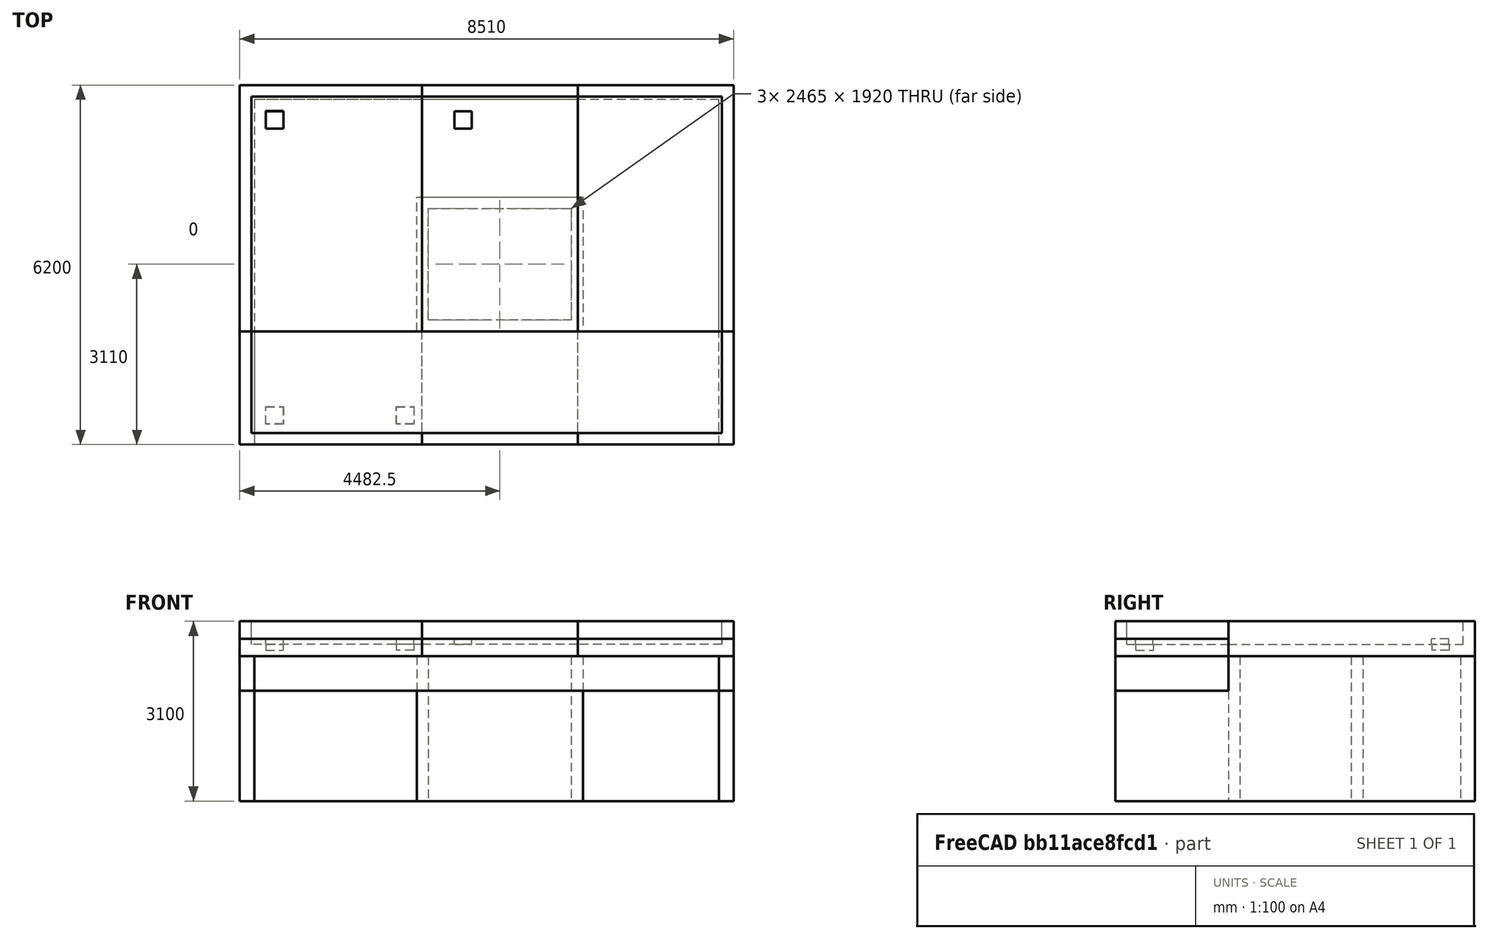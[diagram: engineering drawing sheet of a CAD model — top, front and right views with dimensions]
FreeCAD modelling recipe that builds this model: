
FCSTD DOCUMENT  (FreeCAD 0.21R33694 (Git))
Label: swimmingPool
License: All rights reserved
LicenseURL: http://en.wikipedia.org/wiki/All_rights_reserved
objects: Part::Feature×13, Part::FeaturePython×11, Sketcher::SketchObject×10, Part::Extrusion×10, Image::ImagePlane×3, Part::MultiFuse×3, App::MaterialObjectPython×3, Part::Compound×2, Part::Box×2, Fem::FeaturePython×1, Fem::FemSolverObjectPython×1, Fem::ConstraintFixed×1, Fem::ConstraintForce×1, App::DocumentObjectGroup×1, Fem::FemMeshObjectPython×1, Fem::FemAnalysis×1
note: 51 computed .brp shape members not serialized (recipe doc carries the construction recipe); baked Part::Feature solids carry a one-line shape summary decoded from their .brp

FEATURE [Image::ImagePlane] ImagePlane  label="draufsicht_trh1"
  Placement = pos=(3803,2748,-500) rot=(0,0,1;0rad)
  XSize = 14030.6
  YSize = 11281.2
  expr: XSize = 321.5 * 43.641 mm
  expr: YSize = 258.5 * 43.641 mm
FEATURE [Image::ImagePlane] ImagePlane001  label="grundriss_trh1"
  Placement = pos=(4033,1694,-1000) rot=(0,0,1;0rad)
  XSize = 13245
  YSize = 11006.3
  expr: XSize = 303.5 * 43.641 mm
  expr: YSize = 252.2 * 43.641 mm
FEATURE [Sketcher::SketchObject] Sketch
  FullyConstrained = true
  sketch-geometry (12):
    g0: LineSegment StartX=3050 StartY=4270 StartZ=0 EndX=5915 EndY=4270 EndZ=0
    g1: LineSegment StartX=5915 StartY=4270 StartZ=0 EndX=5915 EndY=1950 EndZ=0
    g2: LineSegment StartX=5915 StartY=1950 StartZ=0 EndX=3050 EndY=1950 EndZ=0
    g3: LineSegment StartX=3050 StartY=1950 StartZ=0 EndX=3050 EndY=4270 EndZ=0
    g4: LineSegment StartX=3250 StartY=4070 StartZ=0 EndX=5715 EndY=4070 EndZ=0
    g5: LineSegment StartX=5715 StartY=4070 StartZ=0 EndX=5715 EndY=2150 EndZ=0
    g6: LineSegment StartX=5715 StartY=2150 StartZ=0 EndX=3250 EndY=2150 EndZ=0
    g7: LineSegment StartX=3250 StartY=2150 StartZ=0 EndX=3250 EndY=4070 EndZ=0
    g8: LineSegment StartX=5715 StartY=4070 StartZ=0 EndX=5715 EndY=4270 EndZ=0
    g9: LineSegment StartX=5715 StartY=2150 StartZ=0 EndX=5715 EndY=1950 EndZ=0
    g10: LineSegment StartX=3250 StartY=2150 StartZ=0 EndX=3050 EndY=2150 EndZ=0
    g11: LineSegment StartX=5715 StartY=2150 StartZ=0 EndX=5915 EndY=2150 EndZ=0
  constraints (36):
    c: Coincident(g0,g1)
    c: Coincident(g1,g2)
    c: Coincident(g2,g3)
    c: Coincident(g3,g0)
    c: Horizontal(g0)
    c: Horizontal(g2)
    c: Vertical(g1)
    c: Vertical(g3)
    c: DistanceY(g-1,g2) = 1950
    c: DistanceX(g0,g0) = 2865
    c: DistanceY(g3,g3) = 2320
    c: Coincident(g4,g5)
    c: Coincident(g5,g6)
    c: Coincident(g6,g7)
    c: Coincident(g7,g4)
    c: Horizontal(g4)
    c: Horizontal(g6)
    c: Vertical(g5)
    c: Vertical(g7)
    c: Coincident(g8,g4)
    c: PointOnObject(g8,g0)
    c: Vertical(g8)
    c: Coincident(g9,g5)
    c: PointOnObject(g9,g2)
    c: Vertical(g9)
    c: Coincident(g10,g6)
    c: PointOnObject(g10,g3)
    c: Coincident(g11,g5)
    c: PointOnObject(g11,g1)
    c: Horizontal(g11)
    c: Horizontal(g10)
    c: Equal(g10,g11)
    c: Equal(g11,g9)
    c: Equal(g9,g8)
    c: DistanceX(g-1,g2) = 3050
    c: DistanceX(g11,g11) = 200
FEATURE [Part::Extrusion] Extrude  label="Fahrstuhlschacht"
  Base = -> Sketch
  Dir = (0,0,-1)
  DirMode = 0
  FaceMakerClass = Part::FaceMakerBullseye
  LengthFwd = 2500
  LengthRev = 0
  Solid = true
  Symmetric = false
FEATURE [Image::ImagePlane] ImagePlane002  label="gwp"
  Placement = pos=(4190,2670,390) rot=(0,0,1;0rad)
  XSize = 9203.05
  YSize = 7710.83
  expr: XSize = 298.5 * 30.831 mm
  expr: YSize = 250.1 * 30.831 mm
FEATURE [Sketcher::SketchObject] Sketch001
  ExternalGeometry = -> [Extrude]
  FullyConstrained = true
  MapMode = 5
  Support = -> [Extrude]
  sketch-geometry (4):
    g0: LineSegment StartX=0 StartY=0 StartZ=0 EndX=3140 EndY=0 EndZ=0
    g1: LineSegment StartX=3140 StartY=0 StartZ=0 EndX=3140 EndY=6200 EndZ=0
    g2: LineSegment StartX=3140 StartY=6200 StartZ=0 EndX=0 EndY=6200 EndZ=0
    g3: LineSegment StartX=0 StartY=6200 StartZ=0 EndX=0 EndY=0 EndZ=0
  constraints (11):
    c: Coincident(g0,g1)
    c: Coincident(g1,g2)
    c: Coincident(g2,g3)
    c: Coincident(g3,g0)
    c: Horizontal(g0)
    c: Horizontal(g2)
    c: Vertical(g1)
    c: Vertical(g3)
    c: Coincident(g0,g-1)
    c: DistanceX(g0,g0) = 3140
    c: DistanceY(g3,g3) = 6200
FEATURE [Part::Extrusion] Extrude001
  Base = -> Sketch001
  Dir = (0,0,1)
  DirMode = 0
  FaceMakerClass = Part::FaceMakerBullseye
  LengthFwd = 200
  LengthRev = 0
  Solid = true
  Symmetric = false
FEATURE [Sketcher::SketchObject] Sketch002
  ExternalGeometry = -> [Extrude001]
  FullyConstrained = true
  MapMode = 5
  Support = -> [Extrude]
  sketch-geometry (5):
    g0: LineSegment StartX=5825 StartY=6200 StartZ=0 EndX=8510 EndY=6200 EndZ=0
    g1: LineSegment StartX=8510 StartY=6200 StartZ=0 EndX=8510 EndY=0 EndZ=0
    g2: LineSegment StartX=8510 StartY=0 StartZ=0 EndX=5825 EndY=0 EndZ=0
    g3: LineSegment StartX=5825 StartY=0 StartZ=0 EndX=5825 EndY=6200 EndZ=0
    g4: LineSegment StartX=3140 StartY=0 StartZ=0 EndX=5825 EndY=0 EndZ=0
  constraints (14):
    c: Coincident(g0,g1)
    c: Coincident(g1,g2)
    c: Coincident(g2,g3)
    c: Coincident(g3,g0)
    c: Horizontal(g0)
    c: Horizontal(g2)
    c: Vertical(g1)
    c: Vertical(g3)
    c: Horizontal(g2,g-3)
    c: Equal(g-4,g1)
    c: Coincident(g4,g-3)
    c: Coincident(g4,g2)
    c: Equal(g4,g2)
    c: DistanceX(g-4,g1) = 8510
FEATURE [Part::Extrusion] Extrude002
  Base = -> Sketch002
  Dir = (0,0,1)
  DirMode = 0
  FaceMakerClass = Part::FaceMakerBullseye
  LengthFwd = 200
  LengthRev = 0
  Solid = true
  Symmetric = false
FEATURE [Sketcher::SketchObject] Sketch003
  ExternalGeometry = -> [Extrude001,Extrude002]
  FullyConstrained = true
  MapMode = 5
  Support = -> [Extrude]
  sketch-geometry (4):
    g0: LineSegment StartX=3140 StartY=6200 StartZ=0 EndX=5825 EndY=6200 EndZ=0
    g1: LineSegment StartX=5825 StartY=6200 StartZ=0 EndX=5825 EndY=0 EndZ=0
    g2: LineSegment StartX=5825 StartY=0 StartZ=0 EndX=3140 EndY=0 EndZ=0
    g3: LineSegment StartX=3140 StartY=0 StartZ=0 EndX=3140 EndY=6200 EndZ=0
  constraints (10):
    c: Coincident(g0,g1)
    c: Coincident(g1,g2)
    c: Coincident(g2,g3)
    c: Coincident(g3,g0)
    c: Horizontal(g0)
    c: Horizontal(g2)
    c: Vertical(g1)
    c: Vertical(g3)
    c: Coincident(g0,g-3)
    c: Coincident(g1,g-4)
FEATURE [Part::Extrusion] Extrude003
  Base = -> Sketch003
  Dir = (0,0,1)
  DirMode = 0
  FaceMakerClass = Part::FaceMakerBullseye
  LengthFwd = 200
  LengthRev = 0
  Solid = true
  Symmetric = false
FEATURE [Sketcher::SketchObject] Sketch004
  ExternalGeometry = -> [Extrude001]
  FullyConstrained = true
  MapMode = 5
  Placement = pos=(0,0,200) rot=(0,0,1;0rad)
  Support = -> [Extrude001]
  sketch-geometry (8):
    g0: LineSegment StartX=0 StartY=0 StartZ=0 EndX=0 EndY=6200 EndZ=0
    g1: LineSegment StartX=0 StartY=6200 StartZ=0 EndX=3140 EndY=6200 EndZ=0
    g2: LineSegment StartX=3140 StartY=6200 StartZ=0 EndX=3140 EndY=6000 EndZ=0
    g3: LineSegment StartX=3140 StartY=6000 StartZ=0 EndX=200 EndY=6000 EndZ=0
    g4: LineSegment StartX=200 StartY=6000 StartZ=0 EndX=200 EndY=200 EndZ=0
    g5: LineSegment StartX=200 StartY=200 StartZ=0 EndX=3140 EndY=200 EndZ=0
    g6: LineSegment StartX=3140 StartY=200 StartZ=0 EndX=3140 EndY=0 EndZ=0
    g7: LineSegment StartX=3140 StartY=0 StartZ=0 EndX=0 EndY=0 EndZ=0
  constraints (21):
    c: Coincident(g-1,g0)
    c: Coincident(g0,g1)
    c: Coincident(g1,g2)
    c: Vertical(g2)
    c: Coincident(g2,g3)
    c: Horizontal(g3)
    c: Coincident(g3,g4)
    c: Vertical(g4)
    c: Coincident(g4,g5)
    c: Coincident(g5,g6)
    c: PointOnObject(g6,g-1)
    c: Vertical(g6)
    c: Coincident(g6,g7)
    c: Coincident(g7,g0)
    c: Horizontal(g5)
    c: Coincident(g0,g-3)
    c: Coincident(g1,g-3)
    c: Equal(g7,g1)
    c: Equal(g2,g6)
    c: DistanceY(g2,g2) = 200
    c: DistanceX(g0,g4) = 200
FEATURE [Part::Extrusion] Extrude004
  Base = -> Sketch004
  Dir = (0,0,1)
  DirMode = 0
  FaceMakerClass = Part::FaceMakerBullseye
  LengthFwd = 400
  LengthRev = 0
  Solid = true
  Symmetric = false
FEATURE [Part::MultiFuse] Fusion  label="trog_links"
  Refine = true
  Shapes = -> [Extrude001,Extrude004]
FEATURE [Sketcher::SketchObject] Sketch005
  ExternalGeometry = -> [Extrude002]
  FullyConstrained = true
  MapMode = 5
  Placement = pos=(0,0,200) rot=(0,0,1;0rad)
  Support = -> [Extrude002]
  sketch-geometry (8):
    g0: LineSegment StartX=5825 StartY=6200 StartZ=0 EndX=8510 EndY=6200 EndZ=0
    g1: LineSegment StartX=8510 StartY=6200 StartZ=0 EndX=8510 EndY=0 EndZ=0
    g2: LineSegment StartX=8510 StartY=0 StartZ=0 EndX=5825 EndY=0 EndZ=0
    g3: LineSegment StartX=5825 StartY=0 StartZ=0 EndX=5825 EndY=200 EndZ=0
    g4: LineSegment StartX=5825 StartY=200 StartZ=0 EndX=8310 EndY=200 EndZ=0
    g5: LineSegment StartX=8310 StartY=200 StartZ=0 EndX=8310 EndY=6000 EndZ=0
    g6: LineSegment StartX=8310 StartY=6000 StartZ=0 EndX=5825 EndY=6000 EndZ=0
    g7: LineSegment StartX=5825 StartY=6000 StartZ=0 EndX=5825 EndY=6200 EndZ=0
  constraints (22):
    c: Coincident(g-3,g0)
    c: Coincident(g0,g-3)
    c: Coincident(g0,g1)
    c: PointOnObject(g1,g-1)
    c: Vertical(g1)
    c: Coincident(g1,g2)
    c: PointOnObject(g2,g-1)
    c: Coincident(g2,g3)
    c: Coincident(g3,g4)
    c: Coincident(g4,g5)
    c: Coincident(g5,g6)
    c: Coincident(g6,g7)
    c: Coincident(g7,g0)
    c: Vertical(g7)
    c: Horizontal(g6)
    c: Horizontal(g4)
    c: Vertical(g5)
    c: Vertical(g3)
    c: Equal(g2,g0)
    c: Equal(g7,g3)
    c: DistanceY(g3,g3) = 200
    c: DistanceX(g4,g1) = 200
FEATURE [Part::Extrusion] Extrude005
  Base = -> Sketch005
  Dir = (0,0,1)
  DirMode = 0
  FaceMakerClass = Part::FaceMakerBullseye
  LengthFwd = 400
  LengthRev = 0
  Solid = true
  Symmetric = false
FEATURE [Part::MultiFuse] Fusion001  label="trog_rechts"
  Refine = true
  Shapes = -> [Extrude005,Extrude002]
FEATURE [Sketcher::SketchObject] Sketch006
  ExternalGeometry = -> [Extrude003]
  FullyConstrained = true
  MapMode = 5
  Placement = pos=(0,0,200) rot=(0,0,1;0rad)
  Support = -> [Extrude003]
  sketch-geometry (8):
    g0: LineSegment StartX=3140 StartY=6200 StartZ=0 EndX=5825 EndY=6200 EndZ=0
    g1: LineSegment StartX=5825 StartY=6200 StartZ=0 EndX=5825 EndY=6000 EndZ=0
    g2: LineSegment StartX=5825 StartY=6000 StartZ=0 EndX=3140 EndY=6000 EndZ=0
    g3: LineSegment StartX=3140 StartY=6000 StartZ=0 EndX=3140 EndY=6200 EndZ=0
    g4: LineSegment StartX=3140 StartY=0 StartZ=0 EndX=5825 EndY=0 EndZ=0
    g5: LineSegment StartX=5825 StartY=0 StartZ=0 EndX=5825 EndY=200 EndZ=0
    g6: LineSegment StartX=5825 StartY=200 StartZ=0 EndX=3140 EndY=200 EndZ=0
    g7: LineSegment StartX=3140 StartY=200 StartZ=0 EndX=3140 EndY=0 EndZ=0
  constraints (22):
    c: Coincident(g0,g1)
    c: Coincident(g1,g2)
    c: Coincident(g2,g3)
    c: Coincident(g3,g0)
    c: Horizontal(g2)
    c: Vertical(g1)
    c: Vertical(g3)
    c: Coincident(g0,g-3)
    c: Coincident(g0,g-3)
    c: DistanceY(g1,g1) = 200
    c: Coincident(g4,g5)
    c: Coincident(g5,g6)
    c: Coincident(g6,g7)
    c: Coincident(g7,g4)
    c: Horizontal(g4)
    c: Horizontal(g6)
    c: Vertical(g5)
    c: Vertical(g7)
    c: PointOnObject(g4,g-1)
    c: Vertical(g6,g2)
    c: Equal(g6,g2)
    c: Equal(g5,g1)
FEATURE [Part::Extrusion] Extrude006
  Base = -> Sketch006
  Dir = (0,0,1)
  DirMode = 0
  FaceMakerClass = Part::FaceMakerBullseye
  LengthFwd = 400
  LengthRev = 0
  Solid = true
  Symmetric = false
FEATURE [Part::MultiFuse] Fusion002  label="trog_mitte"
  Refine = true
  Shapes = -> [Extrude006,Extrude003]
FEATURE [Sketcher::SketchObject] Sketch007
  ExternalGeometry = -> [Fusion001]
  FullyConstrained = true
  sketch-geometry (8):
    g0: LineSegment StartX=0 StartY=0 StartZ=0 EndX=0 EndY=6200 EndZ=0
    g1: LineSegment StartX=0 StartY=6200 StartZ=0 EndX=8510 EndY=6200 EndZ=0
    g2: LineSegment StartX=8510 StartY=6200 StartZ=0 EndX=8510 EndY=0 EndZ=0
    g3: LineSegment StartX=8510 StartY=0 StartZ=0 EndX=8260 EndY=0 EndZ=0
    g4: LineSegment StartX=8260 StartY=0 StartZ=0 EndX=8260 EndY=5950 EndZ=0
    g5: LineSegment StartX=8260 StartY=5950 StartZ=0 EndX=250 EndY=5950 EndZ=0
    g6: LineSegment StartX=250 StartY=5950 StartZ=0 EndX=250 EndY=0 EndZ=0
    g7: LineSegment StartX=250 StartY=0 StartZ=0 EndX=0 EndY=0 EndZ=0
  constraints (21):
    c: Coincident(g-1,g0)
    c: PointOnObject(g0,g-2)
    c: Coincident(g0,g1)
    c: Coincident(g1,g-3)
    c: Horizontal(g1)
    c: Coincident(g1,g2)
    c: Coincident(g2,g-3)
    c: Coincident(g2,g3)
    c: PointOnObject(g3,g-1)
    c: Coincident(g3,g4)
    c: Vertical(g4)
    c: Coincident(g4,g5)
    c: Horizontal(g5)
    c: Coincident(g5,g6)
    c: PointOnObject(g6,g-1)
    c: Vertical(g6)
    c: Coincident(g6,g7)
    c: Coincident(g7,g0)
    c: Equal(g7,g3)
    c: DistanceX(g3,g3) = 250
    c: DistanceY(g4,g1) = 250
FEATURE [Part::Extrusion] Extrude007  label="waende"
  Base = -> Sketch007
  Dir = (0,0,-1)
  DirMode = 0
  FaceMakerClass = Part::FaceMakerBullseye
  LengthFwd = 2500
  LengthRev = 0
  Solid = true
  Symmetric = false
FEATURE [Sketcher::SketchObject] Sketch008
  ExternalGeometry = -> [Fusion]
  FullyConstrained = false
  MapMode = 5
  Placement = pos=(0,0,200) rot=(0,0,1;0rad)
  Support = -> [Fusion]
  sketch-geometry (29):
    g0: LineSegment StartX=450 StartY=650 StartZ=0 EndX=750 EndY=650 EndZ=0
    g1: LineSegment StartX=750 StartY=650 StartZ=0 EndX=750 EndY=350 EndZ=0
    g2: LineSegment StartX=750 StartY=350 StartZ=0 EndX=450 EndY=350 EndZ=0
    g3: LineSegment StartX=450 StartY=350 StartZ=0 EndX=450 EndY=650 EndZ=0
    g4: LineSegment StartX=3000 StartY=350 StartZ=0 EndX=2700 EndY=350 EndZ=0
    g5: LineSegment StartX=2700 StartY=350 StartZ=0 EndX=2700 EndY=650 EndZ=0
    g6: LineSegment StartX=2700 StartY=650 StartZ=0 EndX=3000 EndY=650 EndZ=0
    g7: LineSegment StartX=3000 StartY=650 StartZ=0 EndX=3000 EndY=350 EndZ=0
    g8: LineSegment StartX=3700 StartY=5750 StartZ=0 EndX=4000 EndY=5750 EndZ=0
    g9: LineSegment StartX=4000 StartY=5750 StartZ=0 EndX=4000 EndY=5450 EndZ=0
    g10: LineSegment StartX=4000 StartY=5450 StartZ=0 EndX=3700 EndY=5450 EndZ=0
    g11: LineSegment StartX=3700 StartY=5450 StartZ=0 EndX=3700 EndY=5750 EndZ=0
    g12: LineSegment StartX=450 StartY=5750 StartZ=0 EndX=750 EndY=5750 EndZ=0
    g13: LineSegment StartX=750 StartY=5750 StartZ=0 EndX=750 EndY=5450 EndZ=0
    g14: LineSegment StartX=750 StartY=5450 StartZ=0 EndX=450 EndY=5450 EndZ=0
    g15: LineSegment StartX=450 StartY=5450 StartZ=0 EndX=450 EndY=5750 EndZ=0
    g16: LineSegment StartX=450 StartY=350 StartZ=0 EndX=600 EndY=500 EndZ=0
    g17: LineSegment StartX=600 StartY=500 StartZ=0 EndX=750 EndY=650 EndZ=0
    g18: LineSegment StartX=2700 StartY=650 StartZ=0 EndX=2850 EndY=500 EndZ=0
    g19: LineSegment StartX=2850 StartY=500 StartZ=0 EndX=3000 EndY=350 EndZ=0
    g20: LineSegment StartX=450 StartY=5450 StartZ=0 EndX=600 EndY=5600 EndZ=0
    g21: LineSegment StartX=600 StartY=5600 StartZ=0 EndX=750 EndY=5750 EndZ=0
    g22: LineSegment StartX=3700 StartY=5450 StartZ=0 EndX=3850 EndY=5600 EndZ=0
    g23: LineSegment StartX=3850 StartY=5600 StartZ=0 EndX=4000 EndY=5750 EndZ=0
    g24: LineSegment StartX=200 StartY=5600 StartZ=0 EndX=600 EndY=5600 EndZ=0
    g25: LineSegment StartX=350.289 StartY=5851.34 StartZ=0 EndX=850.289 EndY=5851.34 EndZ=0
    g26: LineSegment StartX=850.289 StartY=5851.34 StartZ=0 EndX=850.289 EndY=5351.34 EndZ=0
    g27: LineSegment StartX=850.289 StartY=5351.34 StartZ=0 EndX=350.289 EndY=5351.34 EndZ=0
    g28: LineSegment StartX=350.289 StartY=5351.34 StartZ=0 EndX=350.289 EndY=5851.34 EndZ=0
  constraints (81):
    c: Coincident(g0,g1)
    c: Coincident(g1,g2)
    c: Coincident(g2,g3)
    c: Coincident(g3,g0)
    c: Horizontal(g0)
    c: Horizontal(g2)
    c: Vertical(g1)
    c: Vertical(g3)
    c: Coincident(g4,g5)
    c: Coincident(g5,g6)
    c: Coincident(g6,g7)
    c: Coincident(g7,g4)
    c: Horizontal(g4)
    c: Horizontal(g6)
    c: Vertical(g5)
    c: Vertical(g7)
    c: Coincident(g8,g9)
    c: Coincident(g9,g10)
    c: Coincident(g10,g11)
    c: Coincident(g11,g8)
    c: Horizontal(g8)
    c: Horizontal(g10)
    c: Vertical(g9)
    c: Vertical(g11)
    c: Coincident(g12,g13)
    c: Coincident(g13,g14)
    c: Coincident(g14,g15)
    c: Coincident(g15,g12)
    c: Horizontal(g12)
    c: Horizontal(g14)
    c: Vertical(g13)
    c: Vertical(g15)
    c: Equal(g10,g11)
    c: Equal(g11,g14)
    c: Equal(g14,g13)
    c: Equal(g13,g2)
    c: Equal(g2,g1)
    c: Equal(g1,g4)
    c: Equal(g4,g7)
    c: DistanceX(g2,g2) = 300
    c: Horizontal(g0,g5)
    c: Coincident(g2,g16)
    c: Coincident(g16,g17)
    c: Coincident(g17,g0)
    c: Coincident(g5,g18)
    c: Coincident(g18,g19)
    c: Coincident(g19,g4)
    c: Equal(g16,g17)
    c: Parallel(g16,g17)
    c: Equal(g19,g18)
    c: Parallel(g19,g18)
    c: DistanceX(g16,g18) = 2250
    c: Coincident(g14,g20)
    c: Coincident(g20,g21)
    c: Coincident(g21,g12)
    c: Equal(g20,g21)
    c: Parallel(g20,g21)
    c: Coincident(g10,g22)
    c: Coincident(g22,g23)
    c: Coincident(g23,g8)
    c: Equal(g22,g23)
    c: Parallel(g22,g23)
    c: Horizontal(g22,g20)
    c: Vertical(g20,g16)
    c: DistanceY(g16,g20) = 5100
    c: DistanceX(g20,g22) = 3250
    c: PointOnObject(g24,g-3)
    c: Coincident(g24,g20)
    c: Horizontal(g24)
    c: DistanceY(g20,g-3) = 400
    c: DistanceX(g24,g24) = 400
    c: Coincident(g25,g26)
    c: Coincident(g26,g27)
    c: Coincident(g27,g28)
    c: Coincident(g28,g25)
    c: Horizontal(g25)
    c: Horizontal(g27)
    c: Vertical(g26)
    c: Vertical(g28)
    c: Equal(g27,g26)
    c: DistanceX(g27,g27) = 500
FEATURE [Part::Extrusion] Extrude008  label="ankerplatten"
  Base = -> Sketch008
  Dir = (0,0,1)
  DirMode = 0
  FaceMakerClass = Part::FaceMakerBullseye
  LengthFwd = 100
  LengthRev = 0
  Solid = true
  Symmetric = false
FEATURE [Sketcher::SketchObject] Sketch009
  FullyConstrained = false
  MapMode = 5
  Placement = pos=(0,0,200) rot=(0,0,1;0rad)
  Support = -> [Fusion]
  sketch-geometry (24):
    g0: LineSegment StartX=447.779 StartY=655.135 StartZ=0 EndX=747.779 EndY=655.135 EndZ=0
    g1: LineSegment StartX=747.779 StartY=655.135 StartZ=0 EndX=747.779 EndY=355.135 EndZ=0
    g2: LineSegment StartX=747.779 StartY=355.135 StartZ=0 EndX=447.779 EndY=355.135 EndZ=0
    g3: LineSegment StartX=447.779 StartY=355.135 StartZ=0 EndX=447.779 EndY=655.135 EndZ=0
    g4: LineSegment StartX=2997.78 StartY=355.135 StartZ=0 EndX=2697.78 EndY=355.135 EndZ=0
    g5: LineSegment StartX=2697.78 StartY=355.135 StartZ=0 EndX=2697.78 EndY=655.135 EndZ=0
    g6: LineSegment StartX=2697.78 StartY=655.135 StartZ=0 EndX=2997.78 EndY=655.135 EndZ=0
    g7: LineSegment StartX=2997.78 StartY=655.135 StartZ=0 EndX=2997.78 EndY=355.135 EndZ=0
    g8: LineSegment StartX=3197.78 StartY=5755.14 StartZ=0 EndX=3497.78 EndY=5755.14 EndZ=0
    g9: LineSegment StartX=3497.78 StartY=5755.14 StartZ=0 EndX=3497.78 EndY=5455.14 EndZ=0
    g10: LineSegment StartX=3497.78 StartY=5455.14 StartZ=0 EndX=3197.78 EndY=5455.14 EndZ=0
    g11: LineSegment StartX=3197.78 StartY=5455.14 StartZ=0 EndX=3197.78 EndY=5755.14 EndZ=0
    g12: LineSegment StartX=447.779 StartY=5755.14 StartZ=0 EndX=747.779 EndY=5755.14 EndZ=0
    g13: LineSegment StartX=747.779 StartY=5755.14 StartZ=0 EndX=747.779 EndY=5455.14 EndZ=0
    g14: LineSegment StartX=747.779 StartY=5455.14 StartZ=0 EndX=447.779 EndY=5455.14 EndZ=0
    g15: LineSegment StartX=447.779 StartY=5455.14 StartZ=0 EndX=447.779 EndY=5755.14 EndZ=0
    g16: LineSegment StartX=447.779 StartY=355.135 StartZ=0 EndX=597.779 EndY=505.135 EndZ=0
    g17: LineSegment StartX=597.779 StartY=505.135 StartZ=0 EndX=747.779 EndY=655.135 EndZ=0
    g18: LineSegment StartX=2697.78 StartY=655.135 StartZ=0 EndX=2847.78 EndY=505.135 EndZ=0
    g19: LineSegment StartX=2847.78 StartY=505.135 StartZ=0 EndX=2997.78 EndY=355.135 EndZ=0
    g20: LineSegment StartX=447.779 StartY=5455.14 StartZ=0 EndX=597.779 EndY=5605.14 EndZ=0
    g21: LineSegment StartX=597.779 StartY=5605.14 StartZ=0 EndX=747.779 EndY=5755.14 EndZ=0
    g22: LineSegment StartX=3197.78 StartY=5455.14 StartZ=0 EndX=3347.78 EndY=5605.14 EndZ=0
    g23: LineSegment StartX=3347.78 StartY=5605.14 StartZ=0 EndX=3497.78 EndY=5755.14 EndZ=0
  constraints (66):
    c: Coincident(g0,g1)
    c: Coincident(g1,g2)
    c: Coincident(g2,g3)
    c: Coincident(g3,g0)
    c: Horizontal(g0)
    c: Horizontal(g2)
    c: Vertical(g1)
    c: Vertical(g3)
    c: Coincident(g4,g5)
    c: Coincident(g5,g6)
    c: Coincident(g6,g7)
    c: Coincident(g7,g4)
    c: Horizontal(g4)
    c: Horizontal(g6)
    c: Vertical(g5)
    c: Vertical(g7)
    c: Coincident(g8,g9)
    c: Coincident(g9,g10)
    c: Coincident(g10,g11)
    c: Coincident(g11,g8)
    c: Horizontal(g8)
    c: Horizontal(g10)
    c: Vertical(g9)
    c: Vertical(g11)
    c: Coincident(g12,g13)
    c: Coincident(g13,g14)
    c: Coincident(g14,g15)
    c: Coincident(g15,g12)
    c: Horizontal(g12)
    c: Horizontal(g14)
    c: Vertical(g13)
    c: Vertical(g15)
    c: Equal(g10,g11)
    c: Equal(g11,g14)
    c: Equal(g14,g13)
    c: Equal(g13,g2)
    c: Equal(g2,g1)
    c: Equal(g1,g4)
    c: Equal(g4,g7)
    c: DistanceX(g2,g2) = 300
    c: Horizontal(g0,g5)
    c: Coincident(g2,g16)
    c: Coincident(g16,g17)
    c: Coincident(g17,g0)
    c: Coincident(g5,g18)
    c: Coincident(g18,g19)
    c: Coincident(g19,g4)
    c: Equal(g16,g17)
    c: Parallel(g16,g17)
    c: Equal(g19,g18)
    c: Parallel(g19,g18)
    c: DistanceX(g16,g18) = 2250
    c: Coincident(g14,g20)
    c: Coincident(g20,g21)
    c: Coincident(g21,g12)
    c: Equal(g20,g21)
    c: Parallel(g20,g21)
    c: Coincident(g10,g22)
    c: Coincident(g22,g23)
    c: Coincident(g23,g8)
    c: Equal(g22,g23)
    c: Parallel(g22,g23)
    c: Horizontal(g22,g20)
    c: Vertical(g20,g16)
    c: DistanceY(g16,g20) = 5100
    c: DistanceX(g20,g22) = 2750
FEATURE [Part::Extrusion] Extrude009  label="lasteinleitung"
  Base = -> Sketch009
  Dir = (0,0,1)
  DirMode = 0
  FaceMakerClass = Part::FaceMakerBullseye
  LengthFwd = 100
  LengthRev = 0
  Reversed = true
  Solid = true
  Symmetric = false
FEATURE [Part::Compound] Compound
FEATURE [Fem::FeaturePython] MeshRegion  # FEM object (typed FeaturePython)
  CharacteristicLength = 50
  References = -> [Compound]
FEATURE [Fem::FemSolverObjectPython] SolverCcxTools  # FEM object (typed FeaturePython)
  AnalysisType = 0
  BeamShellResultOutput3D = true
  BucklingFactors = 1
  EigenmodeHighLimit = 1000000
  EigenmodeLowLimit = 0
  EigenmodesCount = 10
  GeometricalNonlinearity = 0
  IterationsControlParameterCutb = 0.25,0.5,0.75,0.85,,,1.5,
  IterationsControlParameterIter = 4,8,9,200,10,400,,200,,
  IterationsControlParameterTimeUse = false
  IterationsThermoMechMaximum = 2000
  IterationsUserDefinedIncrementations = false
  IterationsUserDefinedTimeStepLength = false
  MaterialNonlinearity = 0
  MatrixSolverType = 1
  SplitInputWriter = true
  ThermoMechSteadyState = true
  TimeEnd = 1
  TimeInitialStep = 0.01
FEATURE [Part::FeaturePython] BooleanFragments  # WARN: FeaturePython — macro-defined, semantics opaque (R4)
  Mode = 2
  Objects = -> [Extrude,Fusion,Fusion001,Fusion002,Extrude007]
  Tolerance = 0
FEATURE [Fem::ConstraintFixed] ConstraintFixed
  NormalDirection = (0,0,-1)
  Normals = (53) [(0,0,-1),(0,0,-1),(0,0,-1),(0,0,-1),(0,0,-1),(0,0,-1),(0,0,-1),(0,0,-1),(0,0,-1),(0,0,-1),(0,0,-1),(0,0,-1),(0,0,-1),(0,0,-1),(0,0,-1),(0,0,-1),+37 more]
  Points = (53) [(0,0,-2500),(8510,0,-2500),(0,688.889,-2500),(8510,688.889,-2500),(0,1377.78,-2500),(8510,1377.78,-2500),(0,2066.67,-2500),(8510,2066.67,-2500),+45 more]
  References = -> [BooleanFragments]
  Scale = 49
FEATURE [Fem::ConstraintForce] ConstraintForce  label="Snow"
  DirectionVector = (0,0,-1)
  Force = 51000
  NormalDirection = (0,0,1)
  Points = (187) [(200,200,200),(788,200,200),(1376,200,200),(1964,200,200),(2552,200,200),(3140,200,200),(200,780,200),(788,780,200),(1376,780,200),(1964,780,200),+177 more]
  References = -> [BooleanFragments]
  Reversed = true
  Scale = 58
FEATURE [Part::Box] Box  label="Cube"
  AttacherType = Attacher::AttachEngine3D
  Height = 1200
  Length = 8510
  Placement = pos=(0,0,-600) rot=(0,0,1;0rad)
  Width = 1950
FEATURE [Part::FeaturePython] Slice  # WARN: FeaturePython — macro-defined, semantics opaque (R4)
  Base = -> BooleanFragments
  Mode = 1
  Tolerance = 0
  Tools = -> [Box]
FEATURE [Part::FeaturePython] Slice_child0  label="Slice.0"  # WARN: FeaturePython — macro-defined, semantics opaque (R4)
  Base = -> Slice
  FilterType = 1
  Invert = false
  OverrideMaxVal = 0
  WindowFrom = 80
  WindowTo = 100
  items = 0
FEATURE [Part::FeaturePython] Slice_child1  label="Slice.1"  # WARN: FeaturePython — macro-defined, semantics opaque (R4)
  Base = -> Slice
  FilterType = 1
  Invert = false
  OverrideMaxVal = 0
  WindowFrom = 80
  WindowTo = 100
  items = 1
FEATURE [App::DocumentObjectGroup] GrExplode_Slice  label="Exploded Slice"
  Group = -> [Slice_child0,Slice_child1]
FEATURE [Part::Box] Box001  label="Cube001"
  AttacherType = Attacher::AttachEngine3D
  Height = 300
  Length = 8510
  Width = 1950
FEATURE [Part::FeaturePython] Slice001  # WARN: FeaturePython — macro-defined, semantics opaque (R4)
  Base = -> GrExplode_Slice
  Mode = 1
  Tolerance = 0
  Tools = -> [Box001]
FEATURE [Part::FeaturePython] Slice001_child0  label="Slice001.0"  # WARN: FeaturePython — macro-defined, semantics opaque (R4)
  Base = -> Slice001
  FilterType = 1
  Invert = false
  OverrideMaxVal = 0
  WindowFrom = 80
  WindowTo = 100
  items = 0
FEATURE [Part::FeaturePython] Slice001_child1  label="Slice001.1"  # WARN: FeaturePython — macro-defined, semantics opaque (R4)
  Base = -> Slice001
  FilterType = 1
  Invert = false
  OverrideMaxVal = 0
  WindowFrom = 80
  WindowTo = 100
  items = 1
FEATURE [Part::FeaturePython] Slice001_child2  label="Slice001.2"  # WARN: FeaturePython — macro-defined, semantics opaque (R4)
  Base = -> Slice001
  FilterType = 1
  Invert = false
  OverrideMaxVal = 0
  WindowFrom = 80
  WindowTo = 100
  items = 2
FEATURE [Part::FeaturePython] Slice001_child3  label="Slice001.3"  # WARN: FeaturePython — macro-defined, semantics opaque (R4)
  Base = -> Slice001
  FilterType = 1
  Invert = false
  OverrideMaxVal = 0
  WindowFrom = 80
  WindowTo = 100
  items = 3
FEATURE [Part::FeaturePython] Slice001_child4  label="Slice001.4"  # WARN: FeaturePython — macro-defined, semantics opaque (R4)
  Base = -> Slice001
  FilterType = 1
  Invert = false
  OverrideMaxVal = 0
  WindowFrom = 80
  WindowTo = 100
  items = 4
FEATURE [Part::Feature] Solid
  shape: bbox 3140 x 1950 x 300 mm, 8 faces (baked)
FEATURE [Part::Feature] Solid001
  shape: bbox 2685 x 1950 x 300 mm, 8 faces (baked)
FEATURE [Part::Feature] Solid002
  shape: bbox 2685 x 200 x 300 mm, 6 faces (baked)
FEATURE [Part::Feature] Solid003
  shape: bbox 3140 x 1950 x 300 mm, 10 faces (baked)
FEATURE [Part::Feature] Solid004
  shape: bbox 2685 x 1950 x 300 mm, 10 faces (baked)
FEATURE [Part::Feature] Solid005
  shape: bbox 2685 x 1950 x 300 mm, 8 faces (baked)
FEATURE [Part::Feature] Solid006
  shape: bbox 250 x 1950 x 600 mm, 6 faces (baked)
FEATURE [Part::Feature] Solid007
  shape: bbox 250 x 1950 x 600 mm, 6 faces (baked)
FEATURE [Part::Feature] Solid008
  shape: bbox 2865 x 2320 x 2500 mm, 13 faces (baked)
FEATURE [Part::Feature] Solid009
  shape: bbox 8510 x 6200 x 2500 mm, 16 faces (baked)
FEATURE [Part::Feature] Solid010
  shape: bbox 3140 x 4250 x 600 mm, 12 faces (baked)
FEATURE [Part::Feature] Solid011
  shape: bbox 2685 x 4250 x 600 mm, 12 faces (baked)
FEATURE [Part::Feature] Solid012
  shape: bbox 2685 x 4250 x 600 mm, 11 faces (baked)
FEATURE [App::MaterialObjectPython] MaterialSolid  label="C30"  # material (typed FeaturePython)
  Category = 0
  Material = AuthorAndLicense=(c) 2013 Yorik van Havre (CC-BY 3.0),CardName=Concrete-Generic,CompressiveStrength=25 MPa,Density=2400 kg/m^3,+7 more (map truncated)
  References = -> [Solid009,Solid010,Solid011,Solid008,Solid012]
FEATURE [Part::Compound] Compound001
  Links = -> [Slice001_child0,Slice001_child1,Slice001_child2,Slice001_child3,Slice001_child4]
FEATURE [App::MaterialObjectPython] MaterialSolid001  # material (typed FeaturePython)
  Category = 0
  Material = AuthorAndLicense=(c) 2013 Yorik van Havre (CC-BY 3.0),CardName=Concrete-Generic,CompressiveStrength=25 MPa,Density=2400 kg/m^3,+7 more (map truncated)
  References = -> [Solid007,Solid004,Solid001,Solid006,Solid003,Solid]
FEATURE [App::MaterialObjectPython] MaterialSolid002  # material (typed FeaturePython)
  Category = 0
  Material = AuthorAndLicense=(c) 2013 Yorik van Havre (CC-BY 3.0),CardName=Concrete-Generic,CompressiveStrength=25 MPa,Density=2400 kg/m^3,+7 more (map truncated)
  References = -> [Solid005,Solid002]
FEATURE [Part::FeaturePython] BooleanFragments001  # WARN: FeaturePython — macro-defined, semantics opaque (R4)
  Mode = 2
  Objects = -> [Solid,Solid001,Solid002,Solid003,Solid004,Solid005,Solid006,Solid007,Solid008,Solid009,Solid010,Solid011,Solid012]
  Tolerance = 0
FEATURE [Fem::FemMeshObjectPython] FEMMeshGmsh  # FEM object (typed FeaturePython)
  Algorithm2D = 0
  Algorithm3D = 0
  CharacteristicLengthMax = 0
  CharacteristicLengthMin = 0
  CoherenceMesh = true
  ElementDimension = 0
  ElementOrder = 1
  GeometryTolerance = 1e-06
  GroupsOfNodes = false
  HighOrderOptimize = 0
  MeshSizeFromCurvature = 12
  OptimizeNetgen = false
  OptimizeStd = true
  Part = -> BooleanFragments001
  RecombinationAlgorithm = 0
  Recombine3DAll = false
  RecombineAll = false
  SecondOrderLinear = false
FEATURE [Fem::FemAnalysis] Analysis
  Group = -> [SolverCcxTools,MaterialSolid,ConstraintFixed,ConstraintForce,MaterialSolid001,MaterialSolid002,FEMMeshGmsh]
